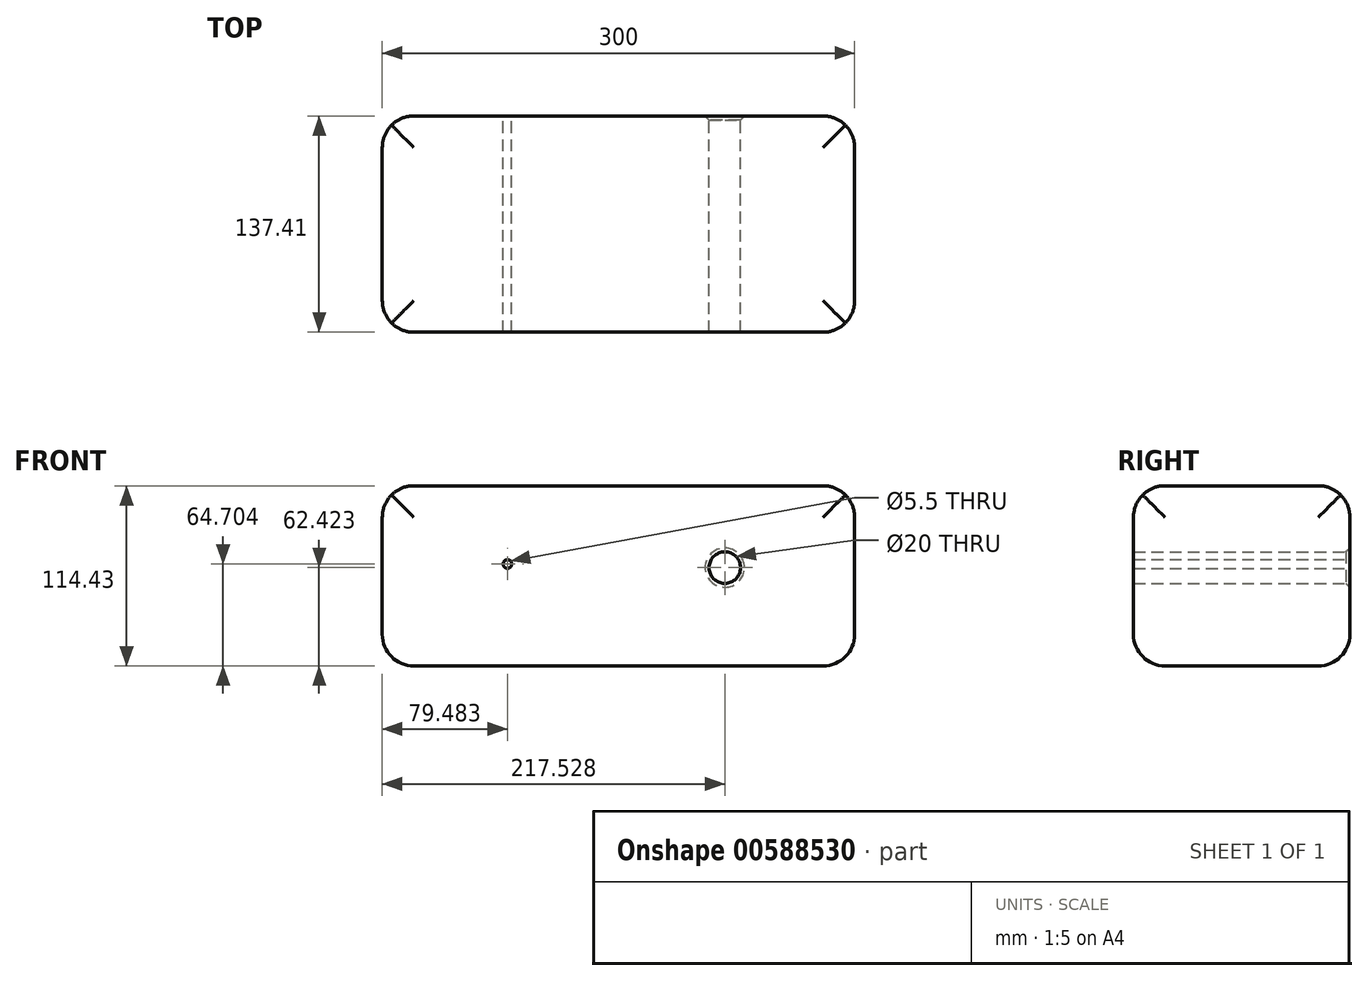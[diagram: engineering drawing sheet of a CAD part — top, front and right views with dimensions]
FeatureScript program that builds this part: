
annotation { "Feature Type Name" : "Feature", "Feature Type Description" : "" }
export const myFeature = defineFeature(function(context is Context, id is Id, definition is map)
    precondition{}
    {
        {
            var Q0;
            Q0=qCreatedBy(makeId("Right.planeOp"),FACE);
            var sketch = newSketch(context, id + "F0", { "sketchPlane" : qUnion([Q0])});
            skLineSegment(sketch, "E0", {"start": v(71.43, 0) * mm, "end": v(0, 0) * mm});
            skLineSegment(sketch, "E1.bottom", {"start": v(-35.15, 243.58) * mm, "end": v(102.26, 243.58) * mm});
            skLineSegment(sketch, "E1.top", {"start": v(-35.15, 129.15) * mm, "end": v(102.26, 129.15) * mm});
            skLineSegment(sketch, "E1.left", {"start": v(-35.15, 243.58) * mm, "end": v(-35.15, 129.15) * mm});
            skLineSegment(sketch, "E1.right", {"start": v(102.26, 243.58) * mm, "end": v(102.26, 129.15) * mm});
            skSolve(sketch);
        }
        {
            var Q0;
            Q0=makeQuery(id+"F0.imprint","IMPRINT",FACE,{"disambiguationData":[TD([[makeQuery(id+"F0.imprint","IMPRINT",EDGE,{"derivedFrom":sQuery(id+"F0.wireOp",EDGE,"E1.bottom")}),-1.0]])]});
            extrude(context, id + "F1", {"entities" : qUnion([Q0]), "depth" : 300 * mm, "offsetDistance" : 25.4 * mm});
        }
        {
            var Q0;
            Q0=makeQuery(id+"F1.opExtrude","SWEPT_FACE",FACE,{"disambiguationData":[OSD([sQuery(id+"F0.wireOp",EDGE,"E1.bottom")])]});
            fillet(context, id + "F2", {"entities" : qUnion([Q0]), "radius" : 20 * mm, "tangentPropagation" : true, "allowEdgeOverflow" : false});
        }
        {
            var Q0;
            Q0=makeQuery(id+"F1.opExtrude","CAP_FACE",FACE,{"disambiguationData":[OSD([sQuery(id+"F0.wireOp",EDGE,"E1.bottom"),sQuery(id+"F0.wireOp",EDGE,"E1.top"),sQuery(id+"F0.wireOp",EDGE,"E1.left"),sQuery(id+"F0.wireOp",EDGE,"E1.right")])],"isStart":true});
            var Q1;
            Q1=makeQuery(id+"F1.opExtrude","CAP_EDGE",EDGE,{"disambiguationData":[OSD([sQuery(id+"F0.wireOp",EDGE,"E1.right")])],"isStart":true});
            var Q2;
            Q2=makeQuery(id+"F1.opExtrude","CAP_EDGE",EDGE,{"disambiguationData":[OSD([sQuery(id+"F0.wireOp",EDGE,"E1.top")])],"isStart":true});
            var Q3;
            {var subQ0=sQuery(id+"F0.wireOp",EDGE,"E1.bottom");Q3=makeQuery(id+"F2.opFillet","BLEND_EDGE",EDGE,{"blendedFrom":[makeQuery(id+"F1.opExtrude","CAP_EDGE",EDGE,{"disambiguationData":[OSD([subQ0])],"isStart":true}),makeQuery(id+"F1.opExtrude","CAP_FACE",FACE,{"disambiguationData":[OSD([subQ0,sQuery(id+"F0.wireOp",EDGE,"E1.top"),sQuery(id+"F0.wireOp",EDGE,"E1.left"),sQuery(id+"F0.wireOp",EDGE,"E1.right")])],"isStart":true})],"blendedInto":[makeQuery(id+"F1.opExtrude","CAP_FACE",FACE,{"disambiguationData":[OSD([subQ0,sQuery(id+"F0.wireOp",EDGE,"E1.top"),sQuery(id+"F0.wireOp",EDGE,"E1.left"),sQuery(id+"F0.wireOp",EDGE,"E1.right")])],"isStart":true})]});}
            var Q4;
            Q4=makeQuery(id+"F1.opExtrude","CAP_EDGE",EDGE,{"disambiguationData":[OSD([sQuery(id+"F0.wireOp",EDGE,"E1.left")])],"isStart":true});
            var Q5;
            Q5=makeQuery(id+"F1.opExtrude","SWEPT_EDGE",EDGE,{"disambiguationData":[OSD([sQuery(id+"F0.wireOp",EDGE,"E1.top"),sQuery(id+"F0.wireOp",EDGE,"E1.left")])]});
            var Q6;
            Q6=makeQuery(id+"F1.opExtrude","SWEPT_EDGE",EDGE,{"disambiguationData":[OSD([sQuery(id+"F0.wireOp",EDGE,"E1.top"),sQuery(id+"F0.wireOp",EDGE,"E1.right")])]});
            var Q7;
            Q7=makeQuery(id+"F1.opExtrude","CAP_EDGE",EDGE,{"disambiguationData":[OSD([sQuery(id+"F0.wireOp",EDGE,"E1.top")])],"isStart":false});
            var Q8;
            Q8=makeQuery(id+"F1.opExtrude","CAP_EDGE",EDGE,{"disambiguationData":[OSD([sQuery(id+"F0.wireOp",EDGE,"E1.right")])],"isStart":false});
            var Q9;
            Q9=makeQuery(id+"F1.opExtrude","CAP_EDGE",EDGE,{"disambiguationData":[OSD([sQuery(id+"F0.wireOp",EDGE,"E1.left")])],"isStart":false});
            fillet(context, id + "F3", {"entities" : qUnion([Q0, Q1, Q2, Q3, Q4, Q5, Q6, Q7, Q8, Q9]), "radius" : 20 * mm, "allowEdgeOverflow" : false});
        }
        {
            var Q0;
            Q0=makeQuery(id+"F1.opExtrude","SWEPT_FACE",FACE,{"disambiguationData":[OSD([sQuery(id+"F0.wireOp",EDGE,"E1.right")])]});
            var sketch = newSketch(context, id + "F4", { "sketchPlane" : qUnion([Q0])});
            skPoint(sketch, "E2", {"position": v(-79.48, 193.85) * mm});
            skPoint(sketch, "E3", {"position": v(-246.35, 184.16) * mm});
            skSolve(sketch);
        }
        {
            var Q0;
            Q0=sQuery(id+"F4.wireOp",VERTEX,"E2");
            var Q1;
            Q1=makeQuery(id+"F1.opExtrude","SWEPT_BODY",BODY,{"disambiguationData":[OSD([sQuery(id+"F0.wireOp",EDGE,"E1.bottom"),sQuery(id+"F0.wireOp",EDGE,"E1.top"),sQuery(id+"F0.wireOp",EDGE,"E1.left"),sQuery(id+"F0.wireOp",EDGE,"E1.right")])]});
            hole(context, id + "F5", {"style" : HoleStyle.SIMPLE, "endStyle" : HoleEndStyle.THROUGH, "standardTappedOrClearance" : lookupTablePath({ "fit" : "Normal", "standard" : "ISO", "size" : "M5", "type" : "Clearance" }), "standardBlindInLast" : lookupTablePath({ "fit" : "Standard", "standard" : "ISO", "size" : "M5", "type" : "Clearance" }), "holeDiameter" : 5.5 * mm, "majorDiameter" : 5 * mm, "isTappedThrough" : true, "tappedDepth" : 12 * mm, "tapClearance" : 3, "locations" : qUnion([Q0]), "scope" : qUnion([Q1])});
        }
        {
            var Q0;
            Q0=makeQuery(id+"F1.opExtrude","SWEPT_FACE",FACE,{"disambiguationData":[OSD([sQuery(id+"F0.wireOp",EDGE,"E1.right")])]});
            var sketch = newSketch(context, id + "F6", { "sketchPlane" : qUnion([Q0])});
            skPoint(sketch, "E4", {"position": v(-217.53, 191.57) * mm});
            skSolve(sketch);
        }
        {
            var Q0;
            Q0=sQuery(id+"F6.wireOp",VERTEX,"E4");
            var Q1;
            Q1=makeQuery(id+"F1.opExtrude","SWEPT_BODY",BODY,{"disambiguationData":[OSD([sQuery(id+"F0.wireOp",EDGE,"E1.bottom"),sQuery(id+"F0.wireOp",EDGE,"E1.top"),sQuery(id+"F0.wireOp",EDGE,"E1.left"),sQuery(id+"F0.wireOp",EDGE,"E1.right")])]});
            hole(context, id + "F7", {"style" : HoleStyle.C_SINK, "endStyle" : HoleEndStyle.THROUGH, "holeDiameter" : 20 * mm, "cSinkDiameter" : 25 * mm, "cSinkAngle" : 90 * degree, "majorDiameter" : 5 * mm, "isTappedThrough" : true, "tappedDepth" : 12 * mm, "tapClearance" : 3, "locations" : qUnion([Q0]), "scope" : qUnion([Q1])});
        }
    });
